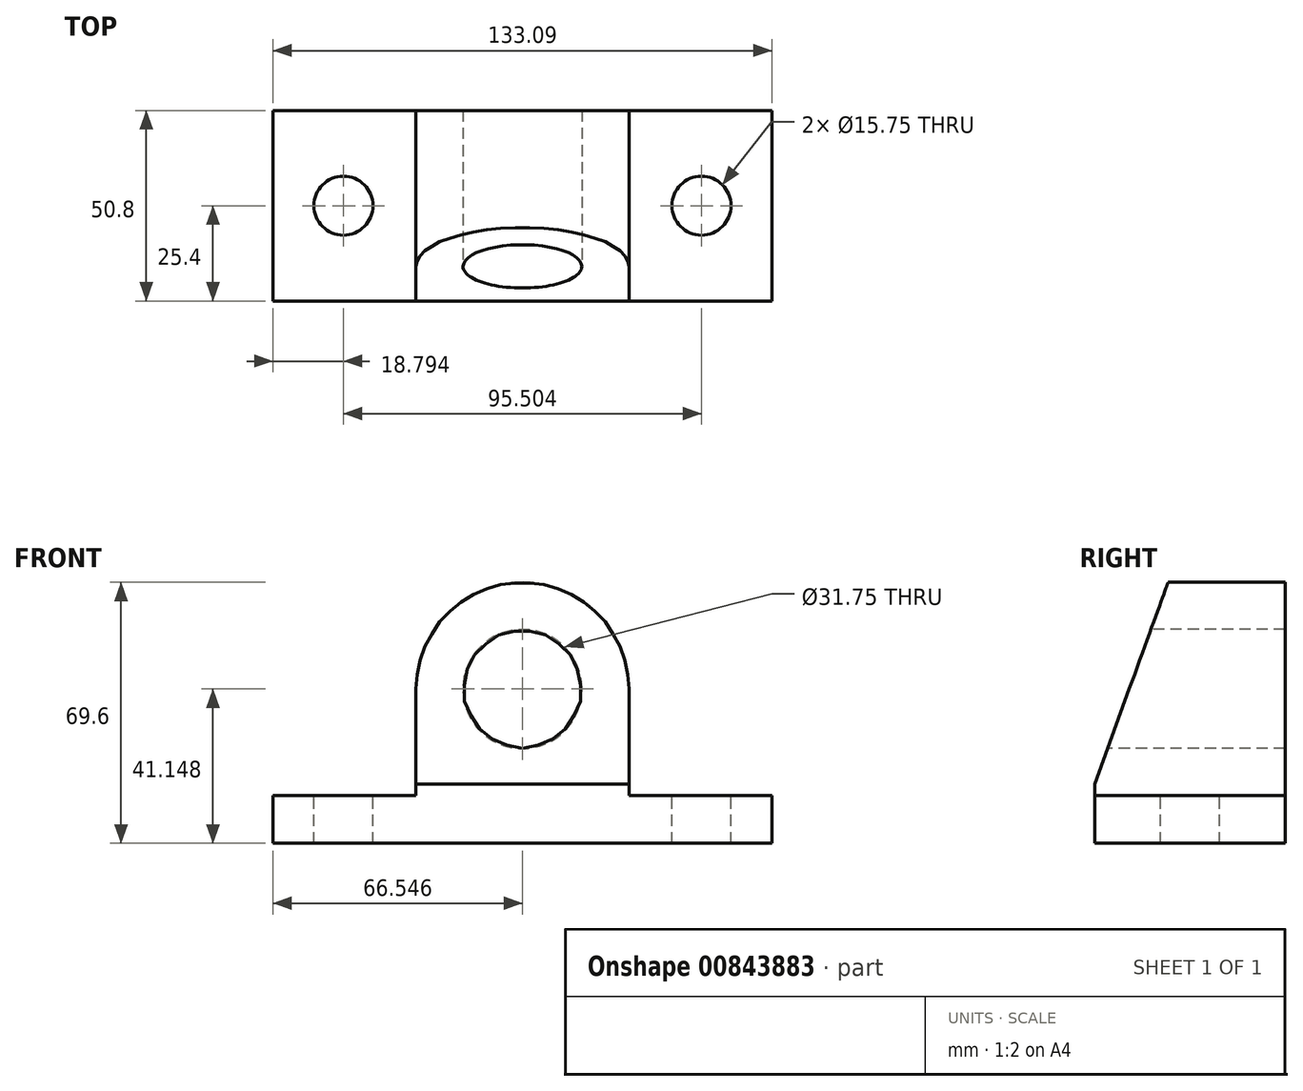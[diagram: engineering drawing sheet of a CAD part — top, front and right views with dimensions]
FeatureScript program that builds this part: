
annotation { "Feature Type Name" : "Feature", "Feature Type Description" : "" }
export const myFeature = defineFeature(function(context is Context, id is Id, definition is map)
    precondition{}
    {
        {
            var Q0;
            Q0=qCreatedBy(makeId("Front.planeOp"),FACE);
            var sketch = newSketch(context, id + "F0", { "sketchPlane" : qUnion([Q0])});
            skLineSegment(sketch, "E0.bottom", {"start": v(66.55, 6.35) * mm, "end": v(-66.55, 6.35) * mm});
            skLineSegment(sketch, "E0.top", {"start": v(66.55, -6.35) * mm, "end": v(-66.55, -6.35) * mm});
            skLineSegment(sketch, "E0.left", {"start": v(66.55, 6.35) * mm, "end": v(66.55, -6.35) * mm});
            skLineSegment(sketch, "E0.right", {"start": v(-66.55, 6.35) * mm, "end": v(-66.55, -6.35) * mm});
            skPoint(sketch, "E0.middle", {"position": v(0, 0) * mm});
            skCircle(sketch, "E1", {"center": v(0, 34.8) * mm, "radius": 15.88 * mm});
            skLineSegment(sketch, "E2.bottom", {"start": v(-28.45, -6.35) * mm, "end": v(28.45, -6.35) * mm});
            skLineSegment(sketch, "E2.left", {"start": v(-28.45, 6.35) * mm, "end": v(-28.45, 34.8) * mm});
            skLineSegment(sketch, "E2.right", {"start": v(28.45, 6.35) * mm, "end": v(28.45, 34.8) * mm});
            skArc(sketch, "E3", {"start": v(-28.45, 34.8) * mm, "mid": v(0, 63.25) * mm, "end": v(28.45, 34.8) * mm});
            skSolve(sketch);
        }
        {
            var Q0;
            {var subQ0=sQuery(id+"F0.wireOp",EDGE,"E0.left");Q0=makeQuery(id+"F0.imprint","IMPRINT",FACE,{"disambiguationData":[TD([[makeQuery(id+"F0.imprint","IMPRINT",EDGE,{"derivedFrom":subQ0}),-1.0]])]});}
            var Q1;
            Q1=makeQuery(id+"F0.imprint","IMPRINT",FACE,{"disambiguationData":[TD([[makeQuery(id+"F0.imprint","IMPRINT",EDGE,{"derivedFrom":sQuery(id+"F0.wireOp",EDGE,"E1")}),-1.0]])]});
            extrude(context, id + "F1", {"entities" : qUnion([Q0, Q1]), "depth" : 50.8 * mm, "offsetDistance" : 25.4 * mm});
        }
        {
            var Q0;
            {var subQ0=sQuery(id+"F0.wireOp",EDGE,"E0.bottom");Q0=makeQuery(id+"F1.opExtrude","SWEPT_FACE",FACE,{"disambiguationData":[OSD([subQ0]),TDD([makeQuery(id+"F0.imprint","IMPRINT",EDGE,{"disambiguationData":[TD([[makeQuery(id+"F0.imprint","INTERSECT",VERTEX,{"derivedFrom":[subQ0,sQuery(id+"F0.wireOp",EDGE,"E0.left")]}),-1.0]])],"derivedFrom":subQ0})])]});}
            var sketch = newSketch(context, id + "F2", { "sketchPlane" : qUnion([Q0])});
            skCircle(sketch, "E4", {"center": v(47.75, -25.4) * mm, "radius": 7.87 * mm});
            skCircle(sketch, "E5", {"center": v(-47.75, -25.4) * mm, "radius": 7.87 * mm});
            skSolve(sketch);
        }
        {
            var Q0;
            Q0=makeQuery(id+"F2.imprint","IMPRINT",FACE,{"disambiguationData":[TD([[makeQuery(id+"F2.imprint","IMPRINT",EDGE,{"derivedFrom":sQuery(id+"F2.wireOp",EDGE,"E4")}),1.0]])]});
            var Q1;
            Q1=makeQuery(id+"F2.imprint","IMPRINT",FACE,{"disambiguationData":[TD([[makeQuery(id+"F2.imprint","IMPRINT",EDGE,{"derivedFrom":sQuery(id+"F2.wireOp",EDGE,"E5")}),1.0]])]});
            extrude(context, id + "F3", {"entities" : qUnion([Q0, Q1]), "operationType" : NewBodyOperationType.REMOVE, "oppositeDirection" : true, "depth" : 12.7 * mm, "offsetDistance" : 25.4 * mm});
        }
        {
            var Q0;
            Q0=makeQuery(id+"F1.opExtrude","SWEPT_FACE",FACE,{"disambiguationData":[OSD([sQuery(id+"F0.wireOp",EDGE,"E2.left")])]});
            var sketch = newSketch(context, id + "F4", { "sketchPlane" : qUnion([Q0])});
            skLineSegment(sketch, "E6.bottom", {"start": v(0, 6.35) * mm, "end": v(50.8, 6.35) * mm});
            skLineSegment(sketch, "E6.top", {"start": v(0, 64.1) * mm, "end": v(50.8, 64.1) * mm});
            skLineSegment(sketch, "E6.left", {"start": v(0, 6.35) * mm, "end": v(0, 64.1) * mm});
            skLineSegment(sketch, "E6.right", {"start": v(50.8, 6.35) * mm, "end": v(50.8, 64.1) * mm});
            skLineSegment(sketch, "E7", {"start": v(0, 6.35) * mm, "end": v(0, 9.4) * mm});
            skLineSegment(sketch, "E8", {"start": v(0, 9.4) * mm, "end": v(19.91, 64.1) * mm});
            skSolve(sketch);
        }
        {
            var Q0;
            {var subQ0=sQuery(id+"F4.wireOp",EDGE,"E6.left");var subQ1=sQuery(id+"F4.wireOp",EDGE,"E6.top");var subQ2=makeQuery(id+"F4.imprint","INTERSECT",VERTEX,{"derivedFrom":[subQ1,subQ0]});Q0=makeQuery(id+"F4.imprint","IMPRINT",FACE,{"disambiguationData":[TD([[makeQuery(id+"F4.imprint","IMPRINT",EDGE,{"disambiguationData":[TD([[subQ2,-1.0]])],"derivedFrom":subQ1}),-1.0]])]});}
            var Q1;
            {var subQ0=sQuery(id+"F4.wireOp",EDGE,"E6.left");var subQ1=makeQuery(id+"F1.opExtrude","SWEPT_EDGE",EDGE,{"disambiguationData":[OSD([sQuery(id+"F0.wireOp",EDGE,"E2.left"),sQuery(id+"F0.wireOp",EDGE,"E3")])]});var subQ2=makeQuery(id+"F4.imprint","INTERSECT",VERTEX,{"derivedFrom":[subQ1,subQ0]});Q1=makeQuery(id+"F4.imprint","IMPRINT",FACE,{"disambiguationData":[TD([[makeQuery(id+"F4.imprint","IMPRINT",EDGE,{"disambiguationData":[TD([[subQ2,1.0]])],"derivedFrom":subQ0}),-1.0]])]});}
            extrude(context, id + "F5", {"entities" : qUnion([Q0, Q1]), "operationType" : NewBodyOperationType.REMOVE, "oppositeDirection" : true, "depth" : 76.2 * mm, "offsetDistance" : 25.4 * mm});
        }
        {
            var Q0;
            Q0=makeQuery(id+"F1.opExtrude","SWEPT_BODY",BODY,{"disambiguationData":[OSD([sQuery(id+"F0.wireOp",EDGE,"E0.bottom"),sQuery(id+"F0.wireOp",EDGE,"E0.top"),sQuery(id+"F0.wireOp",EDGE,"E0.left"),sQuery(id+"F0.wireOp",EDGE,"E0.right"),sQuery(id+"F0.wireOp",EDGE,"E1"),sQuery(id+"F0.wireOp",EDGE,"E2.bottom"),sQuery(id+"F0.wireOp",EDGE,"E2.left"),sQuery(id+"F0.wireOp",EDGE,"E2.right"),sQuery(id+"F0.wireOp",EDGE,"E3")])]});
            var Q1;
            Q1=makeQuery(id+"F1.opExtrude","CAP_EDGE",EDGE,{"disambiguationData":[OSD([sQuery(id+"F0.wireOp",EDGE,"E0.left")])],"isStart":false});
            transform(context, id + "F6", {"entities" : qUnion([Q0]), "transformType" : TransformType.ROTATION, "transformAxis" : qUnion([Q1]), "angle" : 180 * degree, "makeCopy" : false});
        }
    });
